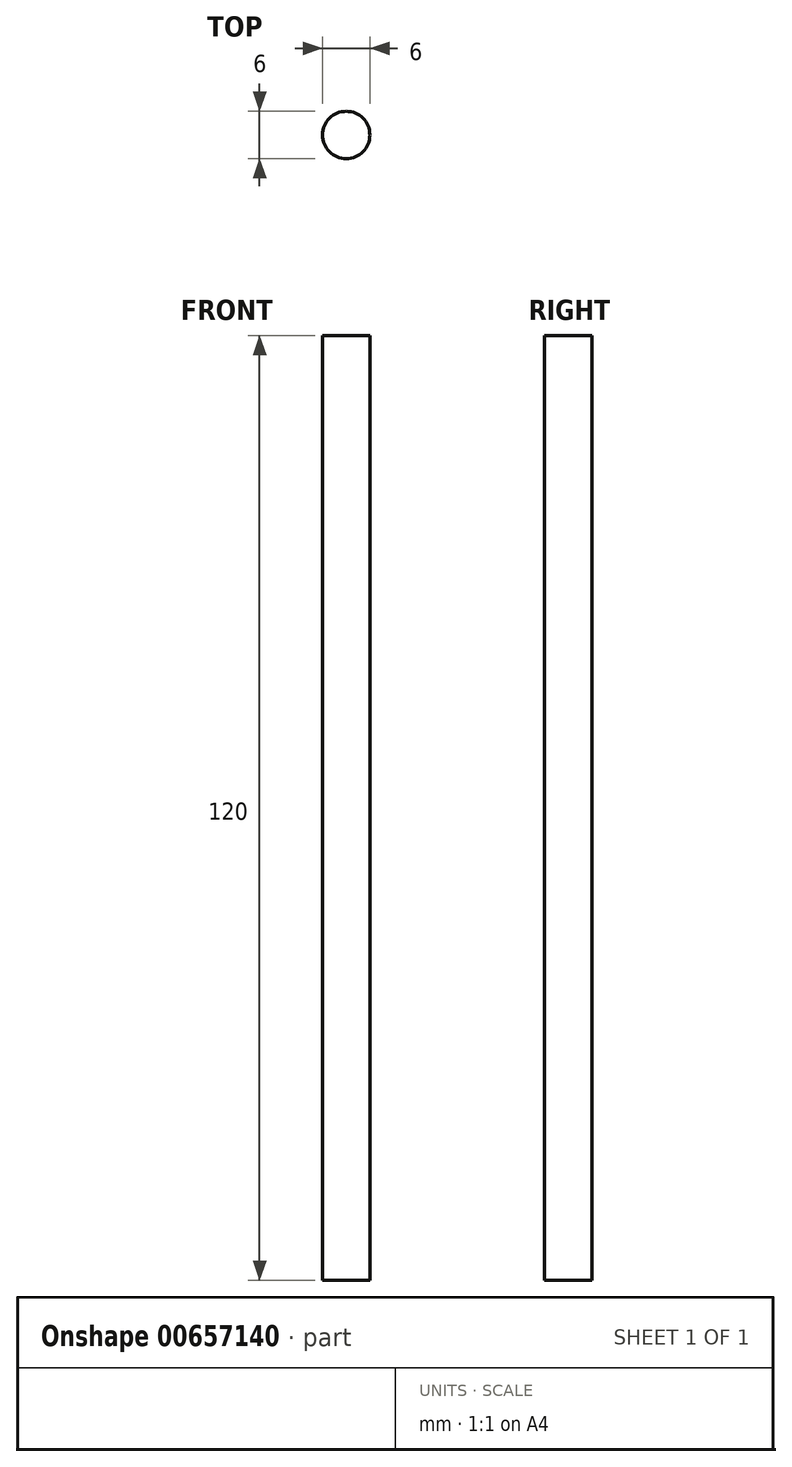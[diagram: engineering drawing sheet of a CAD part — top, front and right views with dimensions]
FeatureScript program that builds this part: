
annotation { "Feature Type Name" : "Feature", "Feature Type Description" : "" }
export const myFeature = defineFeature(function(context is Context, id is Id, definition is map)
    precondition{}
    {
        {
            assignVariable(context, id + "F0", {"name" : "L", "anyValue" : 120});
        }
        {
            var Q0;
            Q0=qCreatedBy(makeId("Top.planeOp"),FACE);
            var sketch = newSketch(context, id + "F1", { "sketchPlane" : qUnion([Q0])});
            skCircle(sketch, "E0", {"center": v(0, 0) * mm, "radius": 3 * mm});
            skSolve(sketch);
        }
        {
            var Q0;
            Q0 = qSketchRegion(id + "F1", true);
            var Q1;
            Q1=sQuery(id+"F1.wireOp",EDGE,"E0");
            extrude(context, id + "F2", {"entities" : qUnion([Q0]), "surfaceEntities" : qUnion([Q1]), "depth" : (getVariable(context, 'L')) * mm, "offsetDistance" : 25 * mm});
        }
    });
